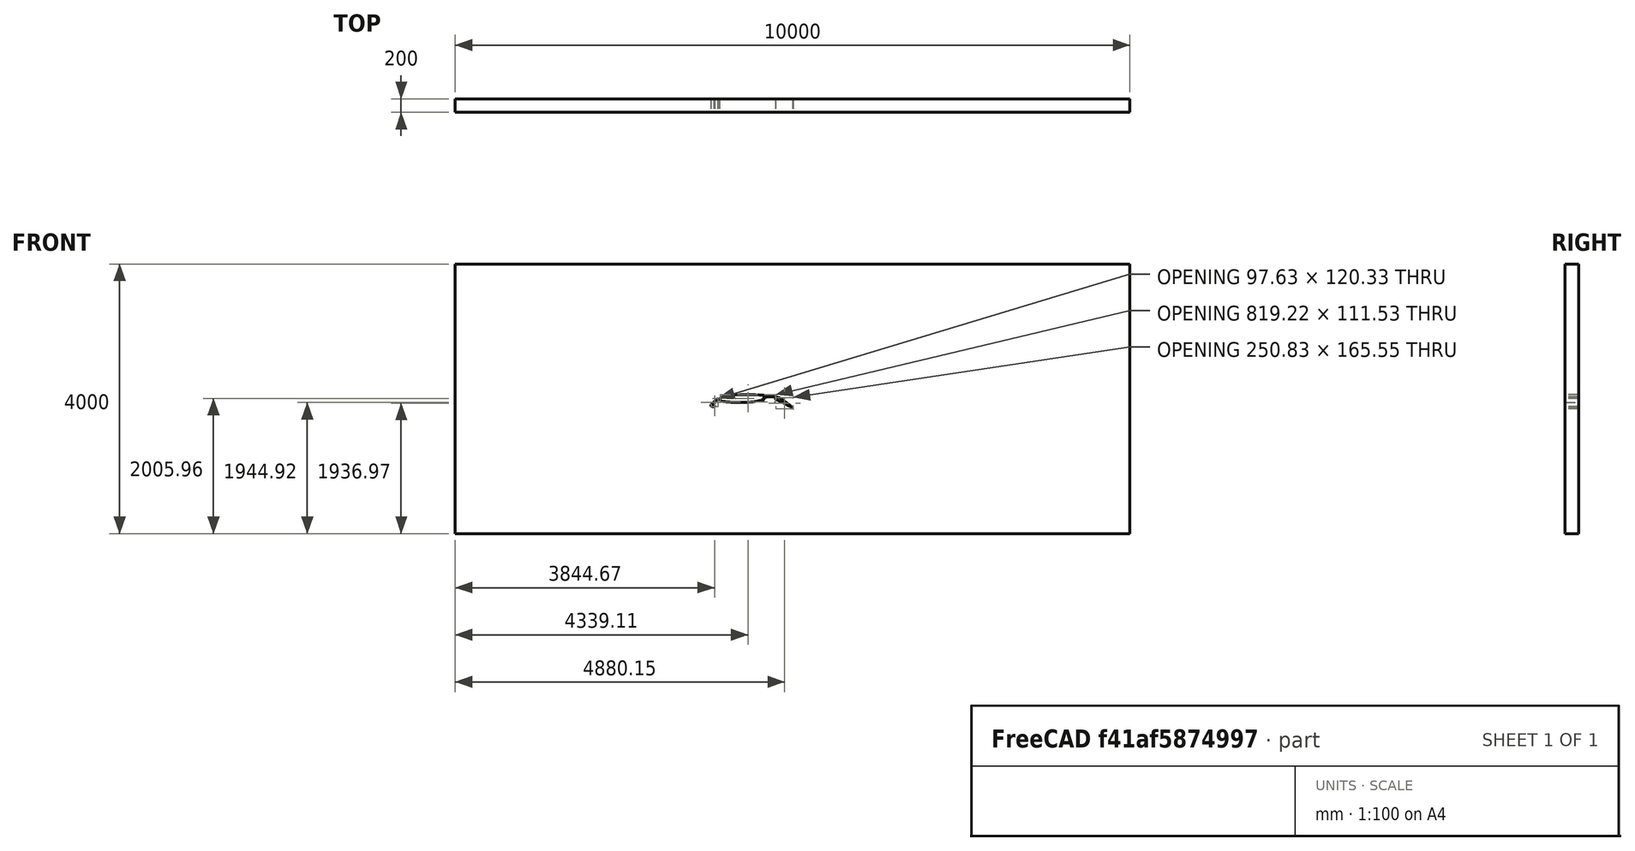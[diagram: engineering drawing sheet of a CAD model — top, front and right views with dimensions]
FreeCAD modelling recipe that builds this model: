
FCSTD DOCUMENT  (FreeCAD 0.20RUnknown)
Label: 30P-30N-Validation
License: All rights reserved
LicenseURL: http://en.wikipedia.org/wiki/All_rights_reserved
objects: Part::FeaturePython×10, Sketcher::SketchObject×2, Part::Extrusion×2, App::DocumentObjectGroupPython×2, Part::Cut×1, App::MaterialObjectPython×1
note: 15 computed .brp shape members not serialized (recipe doc carries the construction recipe); baked Part::Feature solids carry a one-line shape summary decoded from their .brp

FEATURE [Sketcher::SketchObject] Sketch
  FullyConstrained = false
  Placement = pos=(0,0,0) rot=(1,0,0;1.5708rad)
  sketch-geometry (4):
    g0: BSplineCurve PolesCount=201 KnotsCount=199 Degree=3 IsPeriodic=0
    g1: BSplineCurve PolesCount=221 KnotsCount=219 Degree=3 IsPeriodic=0
    g2: BSplineCurve PolesCount=242 KnotsCount=240 Degree=3 IsPeriodic=0
    g3: LineSegment StartX=1128.31 StartY=-145.799 StartZ=0 EndX=1130.86 EndY=-140.497 EndZ=0
  constraints (2):
    c: Coincident(g3,g2)
    c: Coincident(g3,g2)
FEATURE [Sketcher::SketchObject] Sketch001
  FullyConstrained = false
  Placement = pos=(0,0,0) rot=(1,0,0;1.5708rad)
  sketch-geometry (4):
    g0: LineSegment StartX=-3874.71 StartY=2000 StartZ=0 EndX=6125.29 EndY=2000 EndZ=0
    g1: LineSegment StartX=6125.29 StartY=2000 StartZ=0 EndX=6125.29 EndY=-2000 EndZ=0
    g2: LineSegment StartX=6125.29 StartY=-2000 StartZ=0 EndX=-3874.71 EndY=-2000 EndZ=0
    g3: LineSegment StartX=-3874.71 StartY=-2000 StartZ=0 EndX=-3874.71 EndY=2000 EndZ=0
  constraints (10):
    c: Coincident(g0,g1)
    c: Coincident(g1,g2)
    c: Coincident(g2,g3)
    c: Coincident(g3,g0)
    c: Horizontal(g0)
    c: Horizontal(g2)
    c: Vertical(g3)
    c: DistanceX(g0,g0) = 10000
    c: DistanceY(g1,g1) = 4000
    c: Symmetric(g0,g1,g-1)
FEATURE [Part::Extrusion] Extrude001  label="WindTunnelSolid"
  Base = -> Sketch001
  Dir = (0,-1,-3e-16)
  DirMode = 2
  FaceMakerClass = Part::FaceMakerBullseye
  LengthFwd = 200
  LengthRev = 0
  Solid = true
  Symmetric = true
FEATURE [Part::Extrusion] Extrude  label="WingSolid"
  Base = -> Sketch
  Dir = (0,-1,-3e-16)
  DirMode = 2
  FaceMakerClass = Part::FaceMakerBullseye
  LengthFwd = 250
  LengthRev = 0
  Solid = true
  Symmetric = true
FEATURE [Part::Cut] Cut
  Base = -> Extrude001
  Tool = -> Extrude
FEATURE [Part::FeaturePython] PhysicsModel  # WARN: FeaturePython — macro-defined, semantics opaque (R4)
  Flow = 0
  Phase = 0
  Thermal = 0
  Time = 0
  Turbulence = 3
  TurbulenceModel = 0
  gx = 0
  gy = -9800
  gz = 0
FEATURE [App::MaterialObjectPython] FluidProperties  # material (typed FeaturePython)
  Category = 1
  Material = CardName=AirIsothermal; Density=1.20 kg/m^3; Description=Standard air properties at 20 Degrees Celsius and 1 atm; DynamicViscosity=1.80e-5 kg/m/s; Name=Air; Type=Isothermal
FEATURE [Part::FeaturePython] CfdSolver  # WARN: FeaturePython — macro-defined, semantics opaque (R4)
  ConvergenceTol = 0.001
  EndTime = 1
  InputCaseName = case
  MaxIterations = 2000
  Parallel = true
  ParallelCores = 4
  PurgeWrite = 0
  SteadyWriteInterval = 100
  TimeStep = 0.001
  TransientWriteInterval = 0.1
FEATURE [Part::FeaturePython] MeshRefinement  label="Extrusion"  # WARN: FeaturePython — macro-defined, semantics opaque (R4)
  ExpansionRatio = 1
  Extrusion = true
  ExtrusionAngle = 5
  ExtrusionAxisDirection = (1,0,0)
  ExtrusionAxisPoint = (0,0,0)
  ExtrusionLayers = 1
  ExtrusionRatio = 1
  ExtrusionThickness = 100
  ExtrusionType = 2DPlanar
  FirstLayerHeight = 0
  Internal = false
  KeepExistingMesh = false
  NumberLayers = 0
  RefinementThickness = 0
  RegionEdgeRefinement = 1
  RelativeLength = 0.75
  ShapeRefs = -> [Cut]
FEATURE [Part::FeaturePython] MeshRefinement001  label="Wing"  # WARN: FeaturePython — macro-defined, semantics opaque (R4)
  ExpansionRatio = 1.1
  Extrusion = false
  ExtrusionAngle = 5
  ExtrusionAxisDirection = (1,0,0)
  ExtrusionAxisPoint = (0,0,0)
  ExtrusionLayers = 1
  ExtrusionRatio = 1
  ExtrusionThickness = 1
  ExtrusionType = 2DPlanar
  FirstLayerHeight = 0
  Internal = false
  KeepExistingMesh = false
  NumberLayers = 3
  RefinementThickness = 80
  RegionEdgeRefinement = 1
  RelativeLength = 0.1
  ShapeRefs = -> [Cut]
FEATURE [App::DocumentObjectGroupPython] Cut_Mesh  # scripted group (container) (typed FeaturePython)
  CaseName = meshCase
  CellsBetweenLevels = 3
  CharacteristicLengthMax = 20
  ConvertToDualMesh = false
  EdgeRefinement = 1
  ElementDimension = 1
  Group = -> [MeshRefinement,MeshRefinement001]
  ImplicitEdgeDetection = false
  MeshUtility = 0
  NumberOfProcesses = 6
  NumberOfThreads = 0
  Part = -> Cut
  PointInMesh = x=0 m; y=0 m; z=0 m
  STLAngularMeshDensity = 100
  STLRelativeLinearDeflection = 0.001
FEATURE [Part::FeaturePython] CfdFluidBoundary  label="inlet"  # WARN: FeaturePython — macro-defined, semantics opaque (R4)
  BoundarySubType = 5
  BoundaryType = 1
  DefaultBoundary = false
  DissipationRate = 50000000
  HeatFlux = 0
  HeatTransferCoeff = 0
  Intermittency = 1
  MassFlowRate = 0
  NuTilda = 55000000
  PorousBaffleMethod = 0
  Pressure = 0
  PressureDropCoeff = 0
  ReThetat = 1
  ReverseNormal = false
  RoughnessConstant = 0.5
  RoughnessHeight = 0
  ScreenSpacing = 2
  ScreenWireDiameter = 0.2
  ShapeRefs = -> [Cut]
  SlipRatio = 0
  SpecificDissipationRate = 1.5
  Temperature = 290
  ThermalBoundaryType = 0
  TurbulenceInletSpecification = 0
  TurbulenceIntensityPercentage = 1
  TurbulenceLengthScale = 100
  TurbulentKineticEnergy = 4200000
  TurbulentViscosity = 50000000
  Ux = 90000
  Uy = 0
  Uz = 0
  VelocityIsCartesian = true
  VelocityMag = 0
  VolFlowRate = 0
  kEqnTurbulentKineticEnergy = 4200000
  kEqnTurbulentViscosity = 50000000
FEATURE [Part::FeaturePython] InitialiseFields  # WARN: FeaturePython — macro-defined, semantics opaque (R4)
  BoundaryTurb = -> CfdFluidBoundary
  PotentialFlow = true
  PotentialFlowP = true
  Pressure = 0
  ReThetat = 1
  Temperature = 290
  UseInletTemperatureValue = false
  UseInletTurbulenceValues = true
  UseInletUValues = false
  UseOutletPValue = false
  Ux = 0
  Uy = 0
  Uz = 0
  epsilon = 50000000
  gammaInt = 1
  k = 10000
  kEqnNut = 50000000
  kEqnk = 10000
  nuTilda = 55000000
  nut = 50000000
  omega = 57
FEATURE [Part::FeaturePython] CfdFluidBoundary001  label="outlet"  # WARN: FeaturePython — macro-defined, semantics opaque (R4)
  BoundarySubType = 10
  BoundaryType = 2
  DefaultBoundary = false
  DissipationRate = 50000000
  HeatFlux = 0
  HeatTransferCoeff = 0
  Intermittency = 1
  MassFlowRate = 0
  NuTilda = 55000000
  PorousBaffleMethod = 0
  Pressure = 0
  PressureDropCoeff = 0
  ReThetat = 1
  ReverseNormal = false
  RoughnessConstant = 0.5
  RoughnessHeight = 0
  ScreenSpacing = 2
  ScreenWireDiameter = 0.2
  ShapeRefs = -> [Cut]
  SlipRatio = 0
  SpecificDissipationRate = 57
  Temperature = 290
  ThermalBoundaryType = 0
  TurbulenceInletSpecification = 0
  TurbulenceIntensityPercentage = 1
  TurbulenceLengthScale = 100
  TurbulentKineticEnergy = 10000
  TurbulentViscosity = 50000000
  Ux = 0
  Uy = 0
  Uz = 0
  VelocityIsCartesian = true
  VelocityMag = 0
  VolFlowRate = 0
  kEqnTurbulentKineticEnergy = 10000
  kEqnTurbulentViscosity = 50000000
FEATURE [Part::FeaturePython] CfdFluidBoundary002  label="walls"  # WARN: FeaturePython — macro-defined, semantics opaque (R4)
  BoundarySubType = 1
  BoundaryType = 0
  DefaultBoundary = false
  DissipationRate = 50000000
  HeatFlux = 0
  HeatTransferCoeff = 0
  Intermittency = 1
  MassFlowRate = 0
  NuTilda = 55000000
  PorousBaffleMethod = 0
  Pressure = 0
  PressureDropCoeff = 0
  ReThetat = 1
  ReverseNormal = false
  RoughnessConstant = 0.5
  RoughnessHeight = 0
  ScreenSpacing = 2
  ScreenWireDiameter = 0.2
  ShapeRefs = -> [Cut]
  SlipRatio = 0
  SpecificDissipationRate = 57
  Temperature = 290
  ThermalBoundaryType = 0
  TurbulenceInletSpecification = 0
  TurbulenceIntensityPercentage = 1
  TurbulenceLengthScale = 100
  TurbulentKineticEnergy = 10000
  TurbulentViscosity = 50000000
  Ux = 0
  Uy = 0
  Uz = 0
  VelocityIsCartesian = true
  VelocityMag = 0
  VolFlowRate = 0
  kEqnTurbulentKineticEnergy = 10000
  kEqnTurbulentViscosity = 50000000
FEATURE [Part::FeaturePython] CfdFluidBoundary003  label="wing"  # WARN: FeaturePython — macro-defined, semantics opaque (R4)
  BoundarySubType = 0
  BoundaryType = 0
  DefaultBoundary = false
  DissipationRate = 50000000
  HeatFlux = 0
  HeatTransferCoeff = 0
  Intermittency = 1
  MassFlowRate = 0
  NuTilda = 55000000
  PorousBaffleMethod = 0
  Pressure = 0
  PressureDropCoeff = 0
  ReThetat = 1
  ReverseNormal = false
  RoughnessConstant = 0.5
  RoughnessHeight = 0
  ScreenSpacing = 2
  ScreenWireDiameter = 0.2
  ShapeRefs = -> [Cut]
  SlipRatio = 0
  SpecificDissipationRate = 57
  Temperature = 290
  ThermalBoundaryType = 0
  TurbulenceInletSpecification = 0
  TurbulenceIntensityPercentage = 1
  TurbulenceLengthScale = 100
  TurbulentKineticEnergy = 10000
  TurbulentViscosity = 50000000
  Ux = 0
  Uy = 0
  Uz = 0
  VelocityIsCartesian = true
  VelocityMag = 0
  VolFlowRate = 0
  kEqnTurbulentKineticEnergy = 10000
  kEqnTurbulentViscosity = 50000000
FEATURE [Part::FeaturePython] ReportingFunction  label="Coefficients"  # WARN: FeaturePython — macro-defined, semantics opaque (R4)
  AreaRef = 100000
  CentreOfRotation = (0,0,0)
  Cumulative = true
  Direction = (1,0,0)
  Drag = (1,0,0)
  LengthRef = 1000
  Lift = (0,0,1)
  MagnitudeUInf = 90000
  NBins = 0
  Patch = -> CfdFluidBoundary003
  ProbePosition = (0,0,0)
  ReferenceDensity = 1e-09
  ReferencePressure = 5
  ReportingFunctionType = 1
  SampleFieldName = p
  WriteFields = false
FEATURE [App::DocumentObjectGroupPython] CfdAnalysis  # scripted group (container) (typed FeaturePython)
  Group = -> [PhysicsModel,FluidProperties,InitialiseFields,CfdSolver,Cut_Mesh,CfdFluidBoundary,CfdFluidBoundary001,CfdFluidBoundary002,CfdFluidBoundary003,ReportingFunction]
  IsActiveAnalysis = true
  NeedsCaseRewrite = false
  NeedsMeshRerun = false
  NeedsMeshRewrite = true
